FCSTD DOCUMENT  (FreeCAD 0.16R6452 (Git))
Label: Pin_Header_Samtec_HTST
License: All rights reserved
LicenseURL: http://en.wikipedia.org/wiki/All_rights_reserved
objects: Sketcher::SketchObject×2
note: 2 computed .brp shape members not serialized (recipe doc carries the construction recipe); baked Part::Feature solids carry a one-line shape summary decoded from their .brp

FEATURE [Sketcher::SketchObject] Sketch  label="LandPattern_Helper"
  sketch-geometry (49):
    g0: LineSegment StartX=-5.715 StartY=-0.89 StartZ=0 EndX=-4.445 EndY=-0.89 EndZ=0
    g1: LineSegment StartX=-4.445 StartY=-0.89 StartZ=0 EndX=-4.445 EndY=-5.97 EndZ=0
    g2: LineSegment StartX=-4.445 StartY=-5.97 StartZ=0 EndX=-5.715 EndY=-5.97 EndZ=0
    g3: LineSegment StartX=-5.715 StartY=-5.97 StartZ=0 EndX=-5.715 EndY=-0.89 EndZ=0
    g4: LineSegment StartX=-3.175 StartY=-0.89 StartZ=0 EndX=-1.905 EndY=-0.89 EndZ=0
    g5: LineSegment StartX=-1.905 StartY=-0.89 StartZ=0 EndX=-1.905 EndY=-5.97 EndZ=0
    g6: LineSegment StartX=-1.905 StartY=-5.97 StartZ=0 EndX=-3.175 EndY=-5.97 EndZ=0
    g7: LineSegment StartX=-3.175 StartY=-5.97 StartZ=0 EndX=-3.175 EndY=-0.89 EndZ=0
    g8: LineSegment StartX=-0.635 StartY=-0.89 StartZ=0 EndX=0.635 EndY=-0.89 EndZ=0
    g9: LineSegment StartX=0.635 StartY=-0.89 StartZ=0 EndX=0.635 EndY=-5.97 EndZ=0
    g10: LineSegment StartX=0.635 StartY=-5.97 StartZ=0 EndX=-0.635 EndY=-5.97 EndZ=0
    g11: LineSegment StartX=-0.635 StartY=-5.97 StartZ=0 EndX=-0.635 EndY=-0.89 EndZ=0
    g12: LineSegment StartX=1.905 StartY=-0.89 StartZ=0 EndX=3.175 EndY=-0.89 EndZ=0
    g13: LineSegment StartX=3.175 StartY=-0.89 StartZ=0 EndX=3.175 EndY=-5.97 EndZ=0
    g14: LineSegment StartX=3.175 StartY=-5.97 StartZ=0 EndX=1.905 EndY=-5.97 EndZ=0
    g15: LineSegment StartX=1.905 StartY=-5.97 StartZ=0 EndX=1.905 EndY=-0.89 EndZ=0
    g16: LineSegment StartX=4.445 StartY=-0.89 StartZ=0 EndX=5.715 EndY=-0.89 EndZ=0
    g17: LineSegment StartX=5.715 StartY=-0.89 StartZ=0 EndX=5.715 EndY=-5.97 EndZ=0
    g18: LineSegment StartX=5.715 StartY=-5.97 StartZ=0 EndX=4.445 EndY=-5.97 EndZ=0
    g19: LineSegment StartX=4.445 StartY=-5.97 StartZ=0 EndX=4.445 EndY=-0.89 EndZ=0
    g20: LineSegment StartX=-5.715 StartY=5.97 StartZ=0 EndX=-4.445 EndY=5.97 EndZ=0
    g21: LineSegment StartX=-4.445 StartY=5.97 StartZ=0 EndX=-4.445 EndY=0.89 EndZ=0
    g22: LineSegment StartX=-4.445 StartY=0.89 StartZ=0 EndX=-5.715 EndY=0.89 EndZ=0
    g23: LineSegment StartX=-5.715 StartY=0.89 StartZ=0 EndX=-5.715 EndY=5.97 EndZ=0
    g24: LineSegment StartX=-3.175 StartY=5.97 StartZ=0 EndX=-1.905 EndY=5.97 EndZ=0
    g25: LineSegment StartX=-1.905 StartY=5.97 StartZ=0 EndX=-1.905 EndY=0.89 EndZ=0
    g26: LineSegment StartX=-1.905 StartY=0.89 StartZ=0 EndX=-3.175 EndY=0.89 EndZ=0
    g27: LineSegment StartX=-3.175 StartY=0.89 StartZ=0 EndX=-3.175 EndY=5.97 EndZ=0
    g28: LineSegment StartX=-0.635 StartY=5.97 StartZ=0 EndX=0.635 EndY=5.97 EndZ=0
    g29: LineSegment StartX=0.635 StartY=5.97 StartZ=0 EndX=0.635 EndY=0.89 EndZ=0
    g30: LineSegment StartX=0.635 StartY=0.89 StartZ=0 EndX=-0.635 EndY=0.89 EndZ=0
    g31: LineSegment StartX=-0.635 StartY=0.89 StartZ=0 EndX=-0.635 EndY=5.97 EndZ=0
    g32: LineSegment StartX=1.905 StartY=5.97 StartZ=0 EndX=3.175 EndY=5.97 EndZ=0
    g33: LineSegment StartX=3.175 StartY=5.97 StartZ=0 EndX=3.175 EndY=0.89 EndZ=0
    g34: LineSegment StartX=3.175 StartY=0.89 StartZ=0 EndX=1.905 EndY=0.89 EndZ=0
    g35: LineSegment StartX=1.905 StartY=0.89 StartZ=0 EndX=1.905 EndY=5.97 EndZ=0
    g36: LineSegment StartX=4.445 StartY=5.97 StartZ=0 EndX=5.715 EndY=5.97 EndZ=0
    g37: LineSegment StartX=5.715 StartY=5.97 StartZ=0 EndX=5.715 EndY=0.89 EndZ=0
    g38: LineSegment StartX=5.715 StartY=0.89 StartZ=0 EndX=4.445 EndY=0.89 EndZ=0
    g39: LineSegment StartX=4.445 StartY=0.89 StartZ=0 EndX=4.445 EndY=5.97 EndZ=0
    g40: LineSegment [constr] StartX=-5.08 StartY=-3.43 StartZ=0 EndX=-2.54 EndY=-3.43 EndZ=0
    g41: LineSegment [constr] StartX=-2.54 StartY=-3.43 StartZ=0 EndX=0 EndY=-3.43 EndZ=0
    g42: LineSegment [constr] StartX=0 StartY=-3.43 StartZ=0 EndX=2.54 EndY=-3.43 EndZ=0
    g43: LineSegment [constr] StartX=2.54 StartY=-3.43 StartZ=0 EndX=5.08 EndY=-3.43 EndZ=0
    g44: LineSegment [constr] StartX=-5.08 StartY=3.43 StartZ=0 EndX=-2.54 EndY=3.43 EndZ=0
    g45: LineSegment [constr] StartX=-2.54 StartY=3.43 StartZ=0 EndX=0 EndY=3.43 EndZ=0
    g46: LineSegment [constr] StartX=0 StartY=3.43 StartZ=0 EndX=2.54 EndY=3.43 EndZ=0
    g47: LineSegment [constr] StartX=2.54 StartY=3.43 StartZ=0 EndX=5.08 EndY=3.43 EndZ=0
    g48: LineSegment [constr] StartX=0 StartY=3.43 StartZ=0 EndX=0 EndY=-3.43 EndZ=0
  constraints (142):
    c: Coincident(g0,g1)
    c: Coincident(g1,g2)
    c: Coincident(g2,g3)
    c: Coincident(g3,g0)
    c: Horizontal(g0)
    c: Horizontal(g2)
    c: Vertical(g1)
    c: Vertical(g3)
    c: DistanceX(g2) = -1.27
    c: DistanceY(g3) = 5.08
    c: Coincident(g4,g5)
    c: Coincident(g5,g6)
    c: Coincident(g6,g7)
    c: Coincident(g7,g4)
    c: Horizontal(g4)
    c: Horizontal(g6)
    c: Vertical(g5)
    c: Vertical(g7)
    c: Coincident(g8,g9)
    c: Coincident(g9,g10)
    c: Coincident(g10,g11)
    c: Coincident(g11,g8)
    c: Horizontal(g8)
    c: Horizontal(g10)
    c: Vertical(g9)
    c: Vertical(g11)
    c: Coincident(g12,g13)
    c: Coincident(g13,g14)
    c: Coincident(g14,g15)
    c: Coincident(g15,g12)
    c: Horizontal(g12)
    c: Horizontal(g14)
    c: Vertical(g13)
    c: Vertical(g15)
    c: Coincident(g16,g17)
    c: Coincident(g17,g18)
    c: Coincident(g18,g19)
    c: Coincident(g19,g16)
    c: Horizontal(g16)
    c: Horizontal(g18)
    c: Vertical(g17)
    c: Vertical(g19)
    c: Coincident(g20,g21)
    c: Coincident(g21,g22)
    c: Coincident(g22,g23)
    c: Coincident(g23,g20)
    c: Horizontal(g20)
    c: Horizontal(g22)
    c: Vertical(g21)
    c: Vertical(g23)
    c: Coincident(g24,g25)
    c: Coincident(g25,g26)
    c: Coincident(g26,g27)
    c: Coincident(g27,g24)
    c: Horizontal(g24)
    c: Horizontal(g26)
    c: Vertical(g25)
    c: Vertical(g27)
    c: Coincident(g28,g29)
    c: Coincident(g29,g30)
    c: Coincident(g30,g31)
    c: Coincident(g31,g28)
    c: Horizontal(g28)
    c: Horizontal(g30)
    c: Vertical(g29)
    c: Vertical(g31)
    c: Coincident(g32,g33)
    c: Coincident(g33,g34)
    c: Coincident(g34,g35)
    c: Coincident(g35,g32)
    c: Horizontal(g32)
    c: Horizontal(g34)
    c: Vertical(g33)
    c: Vertical(g35)
    c: Coincident(g36,g37)
    c: Coincident(g37,g38)
    c: Coincident(g38,g39)
    c: Coincident(g39,g36)
    c: Horizontal(g36)
    c: Horizontal(g38)
    c: Vertical(g37)
    c: Vertical(g39)
    c: Equal(g2,g38)
    c: Equal(g2,g18)
    c: Equal(g2,g14)
    c: Equal(g2,g10)
    c: Equal(g2,g6)
    c: Equal(g2,g34)
    c: Equal(g2,g30)
    c: Equal(g2,g26)
    c: Equal(g2,g22)
    c: Coincident(g40,g41)
    c: Horizontal(g41)
    c: Coincident(g41,g42)
    c: Horizontal(g42)
    c: Coincident(g42,g43)
    c: Horizontal(g43)
    c: Horizontal(g40)
    c: Equal(g40,g41)
    c: Equal(g41,g42)
    c: Equal(g42,g43)
    c: DistanceX(g40) = 2.54
    c: Equal(g7,g3)
    c: Equal(g3,g11)
    c: Equal(g3,g15)
    c: Equal(g3,g19)
    c: Equal(g3,g23)
    c: Equal(g3,g27)
    c: Equal(g3,g31)
    c: Equal(g3,g35)
    c: Equal(g3,g39)
    c: Horizontal(g44)
    c: Coincident(g44,g45)
    c: Horizontal(g45)
    c: Coincident(g45,g46)
    c: Horizontal(g46)
    c: Coincident(g46,g47)
    c: Horizontal(g47)
    c: Equal(g47,g46)
    c: Equal(g46,g45)
    c: Equal(g45,g44)
    c: Equal(g44,g40)
    c: Symmetric(g0,g2,g40)
    c: Symmetric(g4,g6,g40)
    c: Symmetric(g8,g10,g41)
    c: Symmetric(g12,g14,g42)
    c: Symmetric(g16,g18,g43)
    c: Symmetric(g20,g22,g44)
    c: Symmetric(g24,g26,g44)
    c: Symmetric(g28,g30,g45)
    c: Symmetric(g32,g34,g46)
    c: Symmetric(g36,g38,g47)
    c: Vertical(g48)
    c: Symmetric(g48,g48,g-1)
    c: Coincident(g48,g45)
    c: Coincident(g48,g41)
    c: DistanceY(g36,g17) = -11.94
    c: DistanceY(g16,g37) = 1.78
    c: DistanceY(g47,g43) = -6.86
    c: DistanceY(g-1,g43) = -3.43
    c: DistanceX(g-1,g44) = -5.08
    c: DistanceX(g-1,g44) = -2.54
FEATURE [Sketcher::SketchObject] Sketch001  label="Silkscreen_Helper"
  expr: Constraints[9] = 5 * 2.54mm + 7.62mm
  sketch-geometry (4):
    g0: LineSegment [constr] StartX=10.16 StartY=4.635 StartZ=0 EndX=-10.16 EndY=4.635 EndZ=0
    g1: LineSegment [constr] StartX=-10.16 StartY=4.635 StartZ=0 EndX=-10.16 EndY=-4.635 EndZ=0
    g2: LineSegment [constr] StartX=-10.16 StartY=-4.635 StartZ=0 EndX=10.16 EndY=-4.635 EndZ=0
    g3: LineSegment [constr] StartX=10.16 StartY=-4.635 StartZ=0 EndX=10.16 EndY=4.635 EndZ=0
  constraints (13):
    c: Coincident(g0,g1)
    c: Coincident(g1,g2)
    c: Coincident(g2,g3)
    c: Coincident(g3,g0)
    c: Horizontal(g0)
    c: Horizontal(g2)
    c: Vertical(g1)
    c: Vertical(g3)
    c: DistanceY(g1) = -9.27
    c: DistanceX(g2) = 20.32
    c: Symmetric(g1,g0,g-1)
    c: DistanceX(g1) = -10.16
    c: DistanceY(g1) = -4.635
